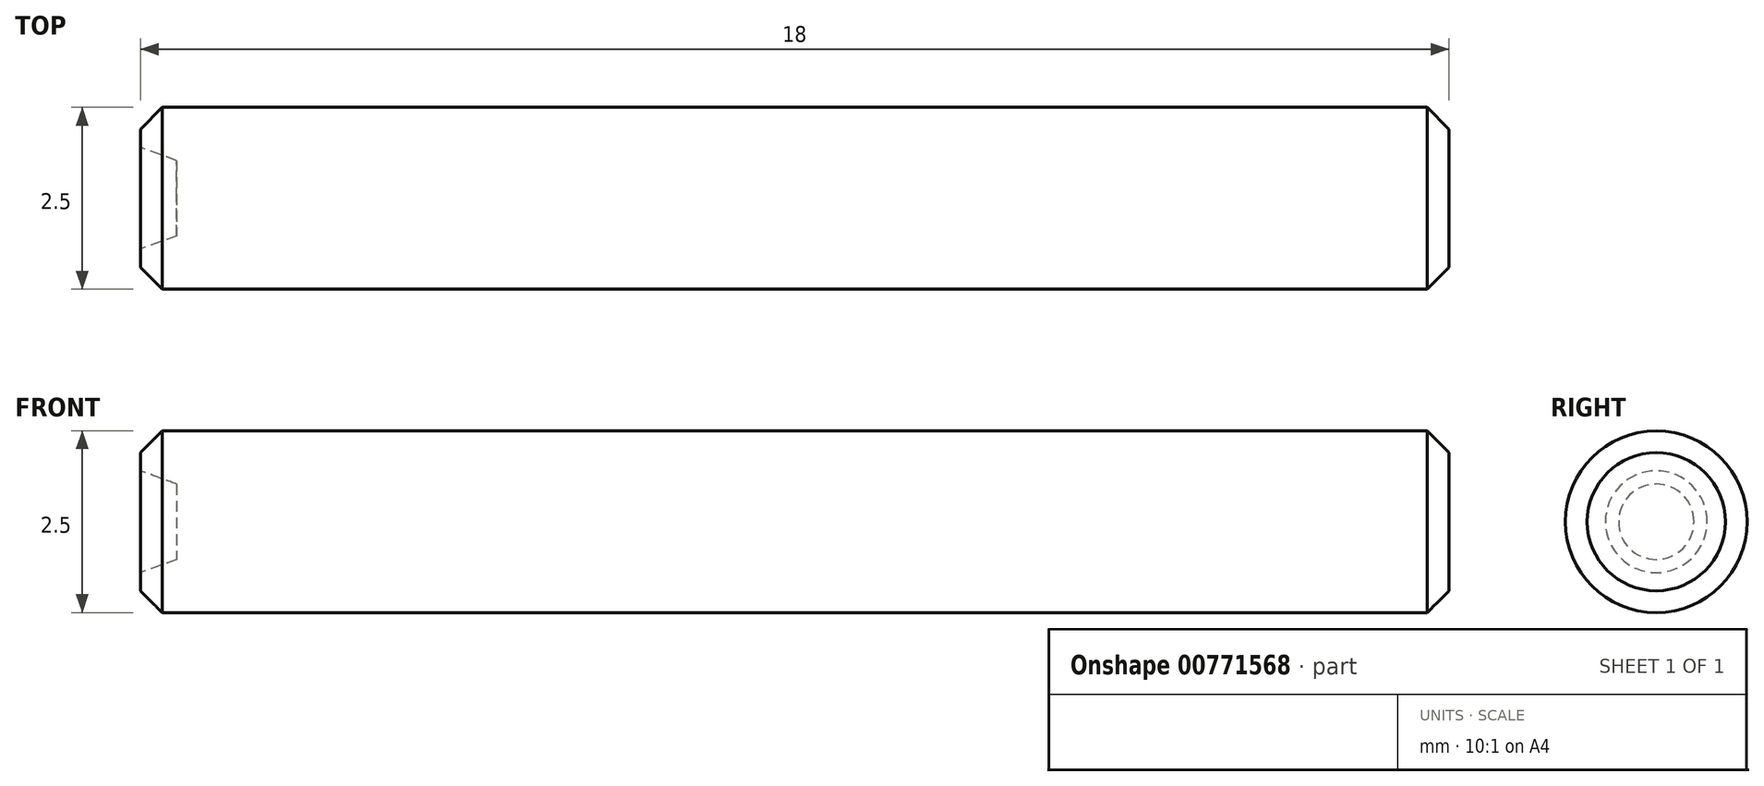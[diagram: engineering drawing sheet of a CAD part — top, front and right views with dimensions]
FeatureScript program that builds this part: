
annotation { "Feature Type Name" : "Feature", "Feature Type Description" : "" }
export const myFeature = defineFeature(function(context is Context, id is Id, definition is map)
    precondition{}
    {
        {
            var Q0;
            Q0=qCreatedBy(makeId("Right.planeOp"),FACE);
            var sketch = newSketch(context, id + "F0", { "sketchPlane" : qUnion([Q0])});
            skCircle(sketch, "E0", {"center": v(0, 0) * mm, "radius": 1.25 * mm});
            skSolve(sketch);
        }
        {
            var Q0;
            Q0 = qSketchRegion(id + "F0", true);
            extrude(context, id + "F1", {"entities" : qUnion([Q0]), "endBound" : BoundingType.SYMMETRIC, "depth" : 18 * mm, "offsetDistance" : 25 * mm});
        }
        {
            var Q0;
            Q0=makeQuery(id+"F1.opExtrude","CAP_EDGE",EDGE,{"disambiguationData":[OSD([sQuery(id+"F0.wireOp",EDGE,"E0")])],"isStart":true});
            var Q1;
            Q1=makeQuery(id+"F1.opExtrude","CAP_EDGE",EDGE,{"disambiguationData":[OSD([sQuery(id+"F0.wireOp",EDGE,"E0")])],"isStart":false});
            chamfer(context, id + "F2", {"entities" : qUnion([Q0, Q1]), "width" : 0.3 * mm, "tangentPropagation" : true});
        }
        {
            var Q0;
            Q0=makeQuery(id+"F1.opExtrude","CAP_FACE",FACE,{"disambiguationData":[OSD([sQuery(id+"F0.wireOp",EDGE,"E0")])],"isStart":true});
            var sketch = newSketch(context, id + "F3", { "sketchPlane" : qUnion([Q0])});
            skCircle(sketch, "E1", {"center": v(0, 0) * mm, "radius": 0.7 * mm});
            skSolve(sketch);
        }
        {
            var Q0;
            Q0 = qSketchRegion(id + "F3", true);
            extrude(context, id + "F4", {"entities" : qUnion([Q0]), "operationType" : NewBodyOperationType.REMOVE, "oppositeDirection" : true, "depth" : 0.5 * mm, "offsetDistance" : 25 * mm, "hasDraft" : true, "draftAngle" : 20 * degree, "draftPullDirection" : true});
        }
    });
